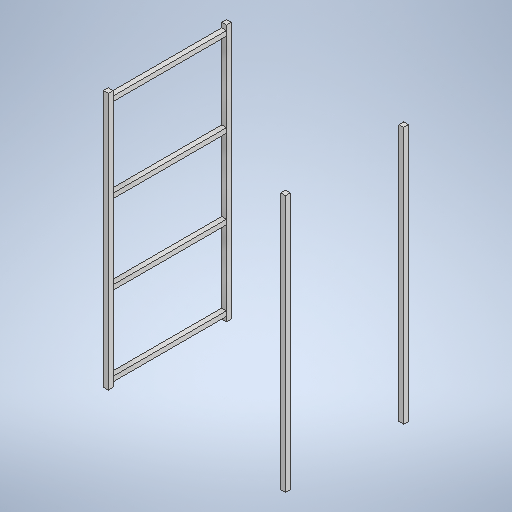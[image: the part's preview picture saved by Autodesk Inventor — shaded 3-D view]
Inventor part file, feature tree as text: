
AUTODESK INVENTOR PART (.ipt)
format: ipt  version: 2025.3 (Build 293356000, 356)  size: 454,144 bytes
history: native  units: mm
features: other x18, sketch x13, extrude x10, mirror x2, pattern_linear x1, move_body x1
ambient origin geometry x8: Origin, YZ Plane, XZ Plane, XY Plane, X Axis, Y Axis, Z Axis, Center Point
bodies: Body1 (feature_tree), Body2 (feature_tree), Body3 (feature_tree), Body4 (feature_tree), Body5 (feature_tree), Body6 (feature_tree), Body7 (feature_tree), Body8 (feature_tree), Body9 (feature_tree), Body10 (feature_tree), Body11 (feature_tree), Body12 (feature_tree), Body13 (feature_tree)
feature tree (45):
  other  "Annotations"
  sketch  "Sketch1"  dims[d0=835.0mm d1=600.0mm d2=600.0mm]
  sketch  "Sketch2"  dims[d3=400.0mm d22=20.0mm d24=820.0mm]
  extrude  "Extrusion2"  Depth=600.0mm
  sketch  "Sketch5"  dims[d34=15.0mm d35=20.0mm d37=370.0mm]
  pattern_linear  "Rectangular Pattern1"  Count1=60  [1 undecoded]
  extrude  "Extrusion3"  Depth=20.0mm
  extrude  "Extrusion4"  Depth=15.0mm
  mirror  "Mirror1"
  extrude  "Extrusion5"  TaperAngle=0.0deg  [1 undecoded]
  extrude  "Extrusion6"  Depth=20.0mm
  mirror  "Mirror2"
  extrude  "Extrusion7"  Depth=15.0mm TaperAngle=0.0deg
  extrude  "Extrusion8"  Depth=15.0mm
  move_body  "Move Body1"
  extrude  "Extrusion9"  Depth=248.333333mm
  extrude  "Extrusion10"  Depth=15.0mm
  extrude  "Extrusion11"  Depth=15.0mm
  sketch  "Sketch4"  dims[d32=15.0mm d33=0.0mm]
  other  "ITEM1"
  sketch  "Sketch Rectangular Pattern2"  dims[d25=15.0mm d26=0.0mm d31=15.0mm]
  other  "Pattern of ITEM1:2"
  other  "ITEM1A"
  other  "ITEM6"
  sketch  "Sketch6"  dims[d38=20.0mm d40=555.0mm d43=15.0mm d44=0.0mm]
  other  "ITEM7"
  other  "Pattern of ITEM7:3"
  other  "ITEM7A"
  sketch  "Sketch7"  dims[d46=15.0mm d47=15.0mm]
  other  "ITEM8"
  sketch  "Sketch8"  dims[d49=15.0mm d52=248.333333mm]
  other  "ITEM2"
  other  "Pattern of ITEM2:4"
  other  "ITEM2A"
  sketch  "Sketch9"  dims[d53=248.333333mm d54=15.0mm]
  other  "ITEM3"
  sketch  "Sketch10"  dims[d55=10.0mm d56=0.0mm d57=15.0mm]
  other  "ITEM4"
  sketch  "Sketch11"  dims[d58=15.0mm]
  other  "ITEM5"
  sketch  "Sketch12"  dims[d59=0.0mm]
  other  "ITEM5A"
  sketch  "Sketch13"  dims[d60=15.0mm d61=15.0mm d62=0.0mm d63=10.0mm d64=0.0mm d65=15.0mm d66=15.0mm d67=248.333333mm d68=15.0mm d69=15.0mm d70=15.0mm d71=15.0mm d72=15.0mm d73=15.0mm d74=0.0mm d75=15.0mm d76=0.0mm d77=15.0mm d78=0.0mm d79=-300.0mm d80=0.0mm d81=-5.0mm d82=15.0mm d83=0.0mm d84=15.0mm d85=0.0mm d86=15.0mm d87=50.0mm d88=15.0mm d89=50.0mm d90=15.0mm d91=0.0mm d92=6.619503mm d93=7.932904mm d94=850.0mm]
  other  "ITEM9"
  other  "Linear Dimension 1"
note: 2 required parameter values undecoded (feature->parameter linkage not recoverable at this tier; creation-order binding heuristic only, values carry confidence <= 0.55)
